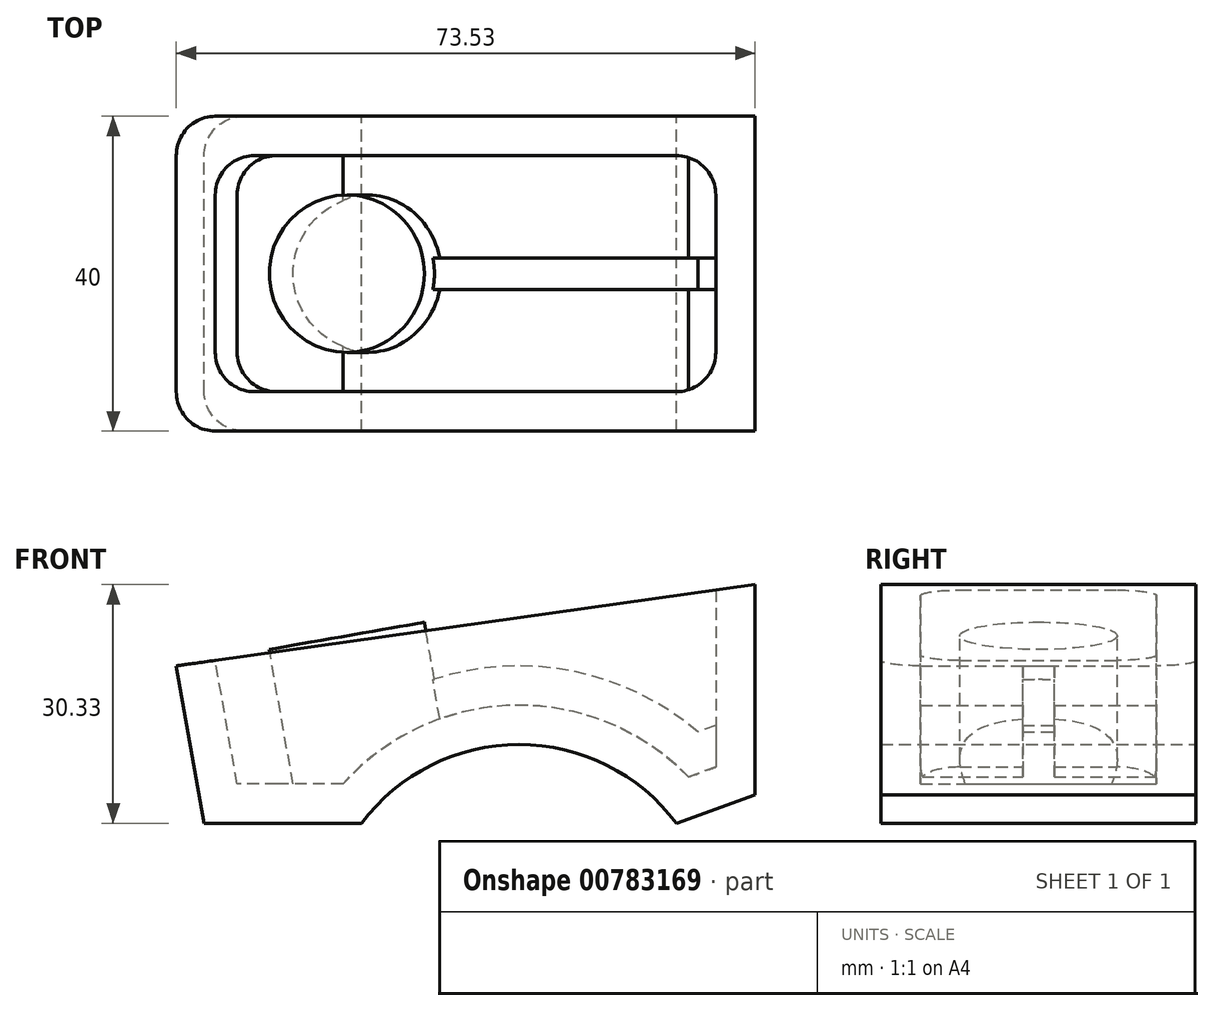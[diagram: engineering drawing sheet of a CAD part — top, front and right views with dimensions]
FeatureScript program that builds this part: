
annotation { "Feature Type Name" : "Feature", "Feature Type Description" : "" }
export const myFeature = defineFeature(function(context is Context, id is Id, definition is map)
    precondition{}
    {
        {
            var Q0;
            Q0=qCreatedBy(makeId("Front.planeOp"),FACE);
            var sketch = newSketch(context, id + "F0", { "sketchPlane" : qUnion([Q0])});
            skLineSegment(sketch, "E0", {"start": v(0, 0) * mm, "end": v(-3.53, 20) * mm});
            skLineSegment(sketch, "E1", {"start": v(-3.53, 20) * mm, "end": v(70, 30.33) * mm});
            skLineSegment(sketch, "E2", {"start": v(70, 30.33) * mm, "end": v(70, 3.64) * mm});
            skLineSegment(sketch, "E3", {"start": v(70, 3.64) * mm, "end": v(60, 0) * mm});
            skLineSegment(sketch, "E4", {"start": v(20, 0) * mm, "end": v(0, 0) * mm});
            skArc(sketch, "E5", {"start": v(60, 0) * mm, "mid": v(40, 10) * mm, "end": v(20, 0) * mm});
            skSolve(sketch);
        }
        {
            var Q0;
            Q0=makeQuery(id+"F0.imprint","IMPRINT",FACE,{"disambiguationData":[TD([[makeQuery(id+"F0.imprint","IMPRINT",EDGE,{"derivedFrom":sQuery(id+"F0.wireOp",EDGE,"E0")}),-1.0]])]});
            extrude(context, id + "F1", {"entities" : qUnion([Q0]), "endBound" : BoundingType.SYMMETRIC, "depth" : 40 * mm, "offsetDistance" : 25 * mm});
        }
        {
            var Q0;
            Q0=makeQuery(id+"F1.opExtrude","SWEPT_FACE",FACE,{"disambiguationData":[OSD([sQuery(id+"F0.wireOp",EDGE,"E1")])]});
            shell(context, id + "F2", {"entities" : qUnion([Q0]), "thickness" : 5 * mm});
        }
        {
            var Q0;
            Q0=qCreatedBy(makeId("Front.planeOp"),FACE);
            var sketch = newSketch(context, id + "F3", { "sketchPlane" : qUnion([Q0])});
            skArc(sketch, "E6.0", {"start": v(62.71, 11.63) * mm, "mid": v(36.14, 19.79) * mm, "end": v(12, 6) * mm});
            skLineSegment(sketch, "E6.1", {"start": v(70, 14.28) * mm, "end": v(62.71, 11.63) * mm});
            skArc(sketch, "E7.0", {"start": v(60, 0) * mm, "mid": v(40, 10) * mm, "end": v(20, 0) * mm});
            skLineSegment(sketch, "E8.0", {"start": v(70, 3.64) * mm, "end": v(60, 0) * mm});
            skLineSegment(sketch, "E9.0", {"start": v(70, 14.28) * mm, "end": v(70, 3.64) * mm});
            skLineSegment(sketch, "E10", {"start": v(12, 6) * mm, "end": v(20, 0) * mm});
            skPoint(sketch, "E11.orphan", {"position": v(70, 30.33) * mm});
            skSolve(sketch);
        }
        {
            var Q0;
            Q0 = qSketchRegion(id + "F3", true);
            extrude(context, id + "F4", {"entities" : qUnion([Q0]), "operationType" : NewBodyOperationType.ADD, "endBound" : BoundingType.SYMMETRIC, "depth" : 4 * mm, "offsetDistance" : 25 * mm});
        }
        {
            var Q0;
            Q0=makeQuery(id+"F1.opExtrude","SWEPT_EDGE",EDGE,{"disambiguationData":[OSD([sQuery(id+"F0.wireOp",EDGE,"E0"),sQuery(id+"F0.wireOp",EDGE,"E1")])]});
            cPlane(context, id + "F5", {"entities" : qUnion([Q0]), "cplaneType" : CPlaneType.LINE_ANGLE, "offset" : 25 * mm, "angle" : 10 * degree, "oppositeDirection" : true, "width" : 150 * mm, "height" : 150 * mm});
        }
        {
            var Q0;
            Q0=qCreatedBy(id+"F5.planeOp",FACE);
            var sketch = newSketch(context, id + "F6", { "sketchPlane" : qUnion([Q0])});
            skCircle(sketch, "E12", {"center": v(22, 0) * mm, "radius": 10 * mm});
            skSolve(sketch);
        }
        {
            var Q0;
            Q0 = qSketchRegion(id + "F6", true);
            extrude(context, id + "F7", {"entities" : qUnion([Q0]), "operationType" : NewBodyOperationType.ADD, "endBound" : BoundingType.UP_TO_NEXT, "oppositeDirection" : true, "depth" : 25 * mm, "offsetDistance" : 25 * mm});
        }
        {
            var Q0;
            {var subQ0=sQuery(id+"F0.wireOp",EDGE,"E0");Q0=makeQuery(id+"F2.opShell","OFFSET_EDGE",EDGE,{"disambiguationData":[OSD([subQ0]),TDD([makeQuery(id+"F1.opExtrude","CAP_EDGE",EDGE,{"disambiguationData":[OSD([subQ0])],"isStart":true})])]});}
            var Q1;
            {var subQ0=sQuery(id+"F0.wireOp",EDGE,"E2");Q1=makeQuery(id+"F2.opShell","OFFSET_EDGE",EDGE,{"disambiguationData":[OSD([subQ0]),TDD([makeQuery(id+"F1.opExtrude","CAP_EDGE",EDGE,{"disambiguationData":[OSD([subQ0])],"isStart":true})])]});}
            var Q2;
            {var subQ0=sQuery(id+"F0.wireOp",EDGE,"E2");Q2=makeQuery(id+"F2.opShell","OFFSET_EDGE",EDGE,{"disambiguationData":[OSD([subQ0]),TDD([makeQuery(id+"F1.opExtrude","CAP_EDGE",EDGE,{"disambiguationData":[OSD([subQ0])],"isStart":false})])]});}
            var Q3;
            {var subQ0=sQuery(id+"F0.wireOp",EDGE,"E0");Q3=makeQuery(id+"F2.opShell","OFFSET_EDGE",EDGE,{"disambiguationData":[OSD([subQ0]),TDD([makeQuery(id+"F1.opExtrude","CAP_EDGE",EDGE,{"disambiguationData":[OSD([subQ0])],"isStart":false})])]});}
            var Q4;
            Q4=makeQuery(id+"F1.opExtrude","CAP_EDGE",EDGE,{"disambiguationData":[OSD([sQuery(id+"F0.wireOp",EDGE,"E0")])],"isStart":false});
            var Q5;
            Q5=makeQuery(id+"F1.opExtrude","CAP_EDGE",EDGE,{"disambiguationData":[OSD([sQuery(id+"F0.wireOp",EDGE,"E0")])],"isStart":true});
            fillet(context, id + "F8", {"entities" : qUnion([Q0, Q1, Q2, Q3, Q4, Q5]), "radius" : 5 * mm, "tangentPropagation" : true, "allowEdgeOverflow" : false});
        }
    });
